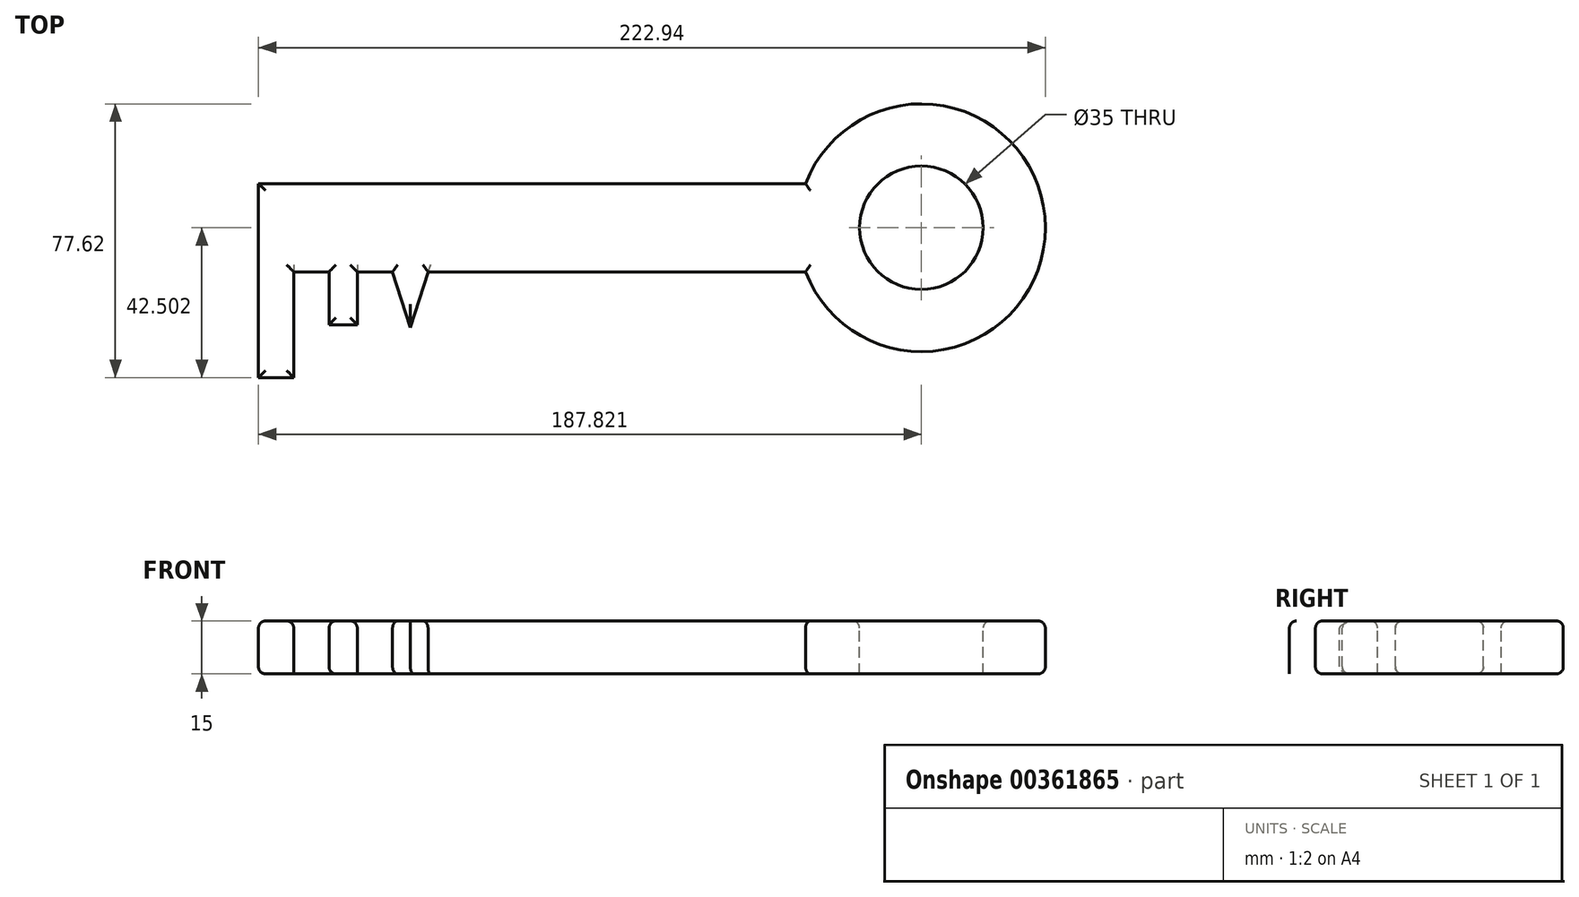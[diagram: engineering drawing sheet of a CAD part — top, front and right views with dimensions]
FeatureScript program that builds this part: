
annotation { "Feature Type Name" : "Feature", "Feature Type Description" : "" }
export const myFeature = defineFeature(function(context is Context, id is Id, definition is map)
    precondition{}
    {
        {
            var Q0;
            Q0=qCreatedBy(makeId("Top.planeOp"),FACE);
            var sketch = newSketch(context, id + "F0", { "sketchPlane" : qUnion([Q0])});
            skLineSegment(sketch, "E0.bottom", {"start": v(-14.84, 11.42) * mm, "end": v(-169.84, 11.42) * mm});
            skLineSegment(sketch, "E0.top", {"start": v(-14.84, 36.42) * mm, "end": v(-169.84, 36.42) * mm});
            skLineSegment(sketch, "E0.right", {"start": v(-169.84, 11.42) * mm, "end": v(-169.84, 36.42) * mm});
            skLineSegment(sketch, "E1.bottom", {"start": v(-169.84, 11.42) * mm, "end": v(-159.84, 11.42) * mm});
            skLineSegment(sketch, "E1.top", {"start": v(-169.84, -18.58) * mm, "end": v(-159.84, -18.58) * mm});
            skLineSegment(sketch, "E1.left", {"start": v(-169.84, 11.42) * mm, "end": v(-169.84, -18.58) * mm});
            skLineSegment(sketch, "E1.right", {"start": v(-159.84, 11.42) * mm, "end": v(-159.84, -18.58) * mm});
            skLineSegment(sketch, "E2.bottom", {"start": v(-149.84, 11.42) * mm, "end": v(-141.84, 11.42) * mm});
            skLineSegment(sketch, "E2.top", {"start": v(-149.84, -3.58) * mm, "end": v(-141.84, -3.58) * mm});
            skLineSegment(sketch, "E2.left", {"start": v(-149.84, 11.42) * mm, "end": v(-149.84, -3.58) * mm});
            skLineSegment(sketch, "E2.right", {"start": v(-141.84, 11.42) * mm, "end": v(-141.84, -3.58) * mm});
            skLineSegment(sketch, "E3", {"start": v(-131.84, 11.42) * mm, "end": v(-121.8, 11.42) * mm});
            skLineSegment(sketch, "E4", {"start": v(-121.8, 11.42) * mm, "end": v(-126.82, -4.35) * mm});
            skLineSegment(sketch, "E5", {"start": v(-126.82, -4.35) * mm, "end": v(-131.84, 11.42) * mm});
            skArc(sketch, "E6", {"start": v(-14.84, 11.42) * mm, "mid": v(53.1, 23.92) * mm, "end": v(-14.84, 36.42) * mm});
            skCircle(sketch, "E7", {"center": v(17.98, 23.92) * mm, "radius": 17.5 * mm});
            skSolve(sketch);
        }
        {
            var Q0;
            Q0 = qSketchRegion(id + "F0", true);
            extrude(context, id + "F1", {"entities" : qUnion([Q0]), "oppositeDirection" : true, "depth" : 15 * mm});
        }
        {
            var Q0;
            Q0=makeQuery(id+"F1.opExtrude","CAP_EDGE",EDGE,{"disambiguationData":[OSD([sQuery(id+"F0.wireOp",EDGE,"E0.top")])],"isStart":true});
            var Q1;
            Q1=makeQuery(id+"F1.opExtrude","CAP_FACE",FACE,{"disambiguationData":[OSD([sQuery(id+"F0.wireOp",EDGE,"E0.bottom"),sQuery(id+"F0.wireOp",EDGE,"E0.top"),sQuery(id+"F0.wireOp",EDGE,"E0.right"),sQuery(id+"F0.wireOp",EDGE,"E1.top"),sQuery(id+"F0.wireOp",EDGE,"E1.left"),sQuery(id+"F0.wireOp",EDGE,"E1.right"),sQuery(id+"F0.wireOp",EDGE,"E2.top"),sQuery(id+"F0.wireOp",EDGE,"E2.left"),sQuery(id+"F0.wireOp",EDGE,"E2.right"),sQuery(id+"F0.wireOp",EDGE,"E4"),sQuery(id+"F0.wireOp",EDGE,"E5"),sQuery(id+"F0.wireOp",EDGE,"E6"),sQuery(id+"F0.wireOp",EDGE,"E7")])],"isStart":true});
            var Q2;
            Q2=makeQuery(id+"F1.opExtrude","CAP_EDGE",EDGE,{"disambiguationData":[OSD([sQuery(id+"F0.wireOp",EDGE,"E6")])],"isStart":true});
            var Q3;
            Q3=makeQuery(id+"F1.opExtrude","CAP_EDGE",EDGE,{"disambiguationData":[OSD([sQuery(id+"F0.wireOp",EDGE,"E7")])],"isStart":true});
            var Q4;
            Q4=makeQuery(id+"F1.opExtrude","CAP_EDGE",EDGE,{"disambiguationData":[OSD([sQuery(id+"F0.wireOp",EDGE,"E4")])],"isStart":true});
            var Q5;
            Q5=makeQuery(id+"F1.opExtrude","CAP_EDGE",EDGE,{"disambiguationData":[OSD([sQuery(id+"F0.wireOp",EDGE,"E2.right")])],"isStart":true});
            var Q6;
            Q6=makeQuery(id+"F1.opExtrude","CAP_EDGE",EDGE,{"disambiguationData":[OSD([sQuery(id+"F0.wireOp",EDGE,"E2.top")])],"isStart":true});
            var Q7;
            Q7=makeQuery(id+"F1.opExtrude","CAP_EDGE",EDGE,{"disambiguationData":[OSD([sQuery(id+"F0.wireOp",EDGE,"E1.right")])],"isStart":true});
            var Q8;
            Q8=makeQuery(id+"F1.opExtrude","CAP_EDGE",EDGE,{"disambiguationData":[OSD([sQuery(id+"F0.wireOp",EDGE,"E1.top")])],"isStart":true});
            var Q9;
            Q9=makeQuery(id+"F1.opExtrude","CAP_EDGE",EDGE,{"disambiguationData":[OSD([sQuery(id+"F0.wireOp",EDGE,"E0.right"),sQuery(id+"F0.wireOp",EDGE,"E1.left")])],"isStart":true});
            var Q10;
            Q10=makeQuery(id+"F1.opExtrude","CAP_EDGE",EDGE,{"disambiguationData":[OSD([sQuery(id+"F0.wireOp",EDGE,"E0.top")])],"isStart":false});
            var Q11;
            {var subQ0=sQuery(id+"F0.wireOp",EDGE,"E0.bottom");Q11=makeQuery(id+"F1.opExtrude","CAP_EDGE",EDGE,{"disambiguationData":[OSD([subQ0]),TDD([makeQuery(id+"F0.imprint","IMPRINT",EDGE,{"disambiguationData":[TD([[makeQuery(id+"F0.imprint","INTERSECT",VERTEX,{"derivedFrom":[subQ0,sQuery(id+"F0.wireOp",EDGE,"E6")]}),-1.0]])],"derivedFrom":subQ0})])],"isStart":false});}
            var Q12;
            Q12=makeQuery(id+"F1.opExtrude","CAP_EDGE",EDGE,{"disambiguationData":[OSD([sQuery(id+"F0.wireOp",EDGE,"E6")])],"isStart":false});
            var Q13;
            Q13=makeQuery(id+"F1.opExtrude","CAP_EDGE",EDGE,{"disambiguationData":[OSD([sQuery(id+"F0.wireOp",EDGE,"E5")])],"isStart":false});
            var Q14;
            {var subQ0=sQuery(id+"F0.wireOp",EDGE,"E0.bottom");Q14=makeQuery(id+"F1.opExtrude","CAP_EDGE",EDGE,{"disambiguationData":[OSD([subQ0]),TDD([makeQuery(id+"F0.imprint","IMPRINT",EDGE,{"disambiguationData":[TD([[makeQuery(id+"F0.imprint","INTERSECT",VERTEX,{"derivedFrom":[subQ0,sQuery(id+"F0.wireOp",EDGE,"E2.bottom"),sQuery(id+"F0.wireOp",EDGE,"E2.right")]}),1.0]])],"derivedFrom":subQ0})])],"isStart":false});}
            var Q15;
            {var subQ0=sQuery(id+"F0.wireOp",EDGE,"E0.bottom");Q15=makeQuery(id+"F1.opExtrude","CAP_EDGE",EDGE,{"disambiguationData":[OSD([subQ0]),TDD([makeQuery(id+"F0.imprint","IMPRINT",EDGE,{"disambiguationData":[TD([[makeQuery(id+"F0.imprint","INTERSECT",VERTEX,{"derivedFrom":[subQ0,sQuery(id+"F0.wireOp",EDGE,"E1.bottom"),sQuery(id+"F0.wireOp",EDGE,"E1.right")]}),1.0]])],"derivedFrom":subQ0})])],"isStart":false});}
            var Q16;
            Q16=makeQuery(id+"F1.opExtrude","CAP_EDGE",EDGE,{"disambiguationData":[OSD([sQuery(id+"F0.wireOp",EDGE,"E2.left")])],"isStart":false});
            var Q17;
            Q17=makeQuery(id+"F1.opExtrude","CAP_EDGE",EDGE,{"disambiguationData":[OSD([sQuery(id+"F0.wireOp",EDGE,"E2.top")])],"isStart":false});
            var Q18;
            Q18=makeQuery(id+"F1.opExtrude","CAP_EDGE",EDGE,{"disambiguationData":[OSD([sQuery(id+"F0.wireOp",EDGE,"E0.right"),sQuery(id+"F0.wireOp",EDGE,"E1.left")])],"isStart":false});
            fillet(context, id + "F2", {"entities" : qUnion([Q0, Q1, Q2, Q3, Q4, Q5, Q6, Q7, Q8, Q9, Q10, Q11, Q12, Q13, Q14, Q15, Q16, Q17, Q18]), "radius" : 2 * mm, "tangentPropagation" : true, "allowEdgeOverflow" : false});
        }
    });
